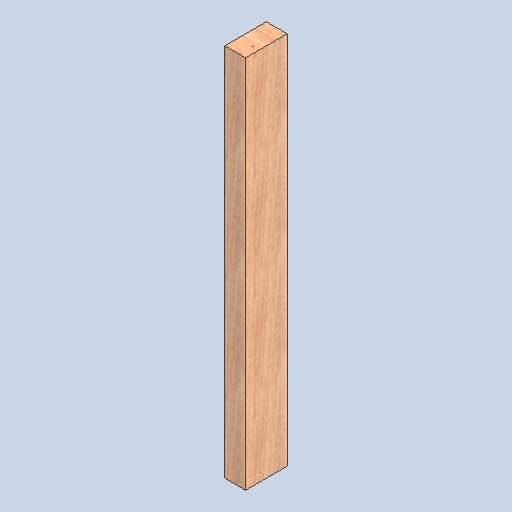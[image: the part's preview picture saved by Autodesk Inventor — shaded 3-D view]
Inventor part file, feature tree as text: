
AUTODESK INVENTOR PART (.ipt)
format: ipt  version: 2025 (Build 290162000, 162)  size: 151,552 bytes
history: native  units: in
note: dims shown in document units (in); Inventor stores cm internally (conversion verified against a paired STEP export)
features: other x3, sketch x1
ambient origin geometry x8: Origin, YZ Plane, XZ Plane, XY Plane, X Axis, Y Axis, Z Axis, Center Point
bodies: Solid1 (feature_tree)
feature tree (4):
  other  "2x4x36.ipt"
  other  "Solid1::2x4x36.ipt"
  other  "TaggingFeature1"
  sketch  "Sketch1"  dims[d0=0.3937in]
